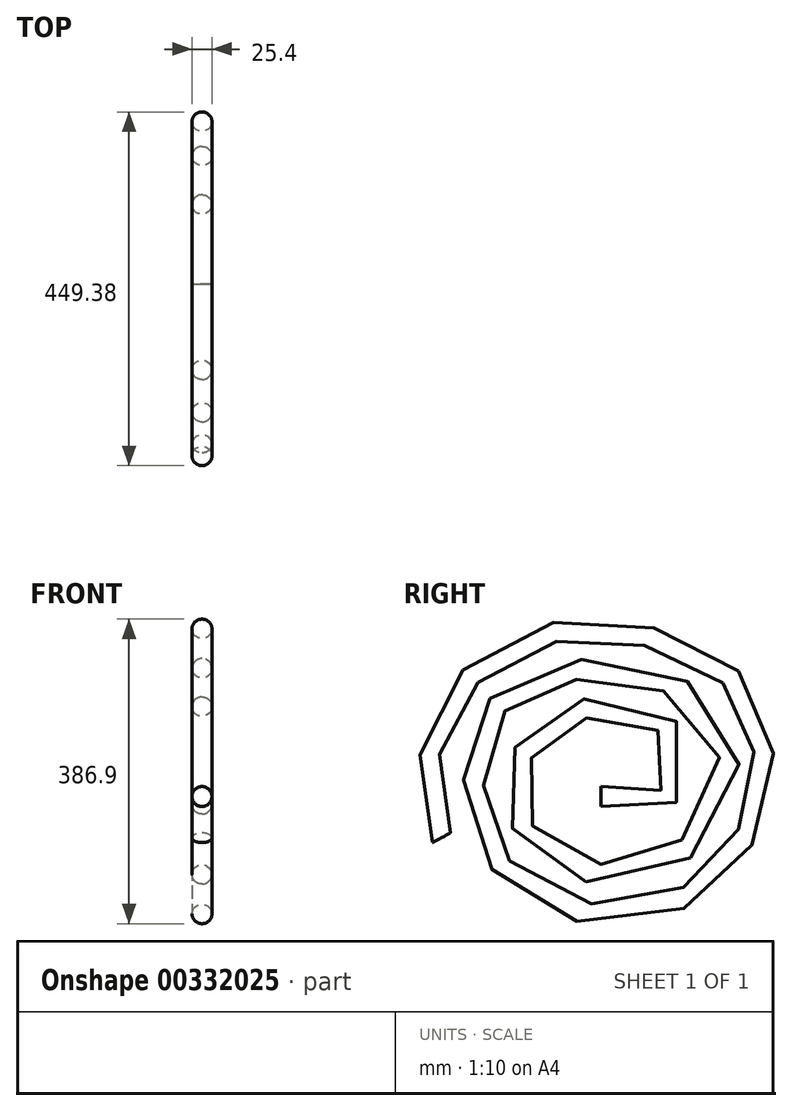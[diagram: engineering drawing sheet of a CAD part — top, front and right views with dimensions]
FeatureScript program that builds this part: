
annotation { "Feature Type Name" : "Feature", "Feature Type Description" : "" }
export const myFeature = defineFeature(function(context is Context, id is Id, definition is map)
    precondition{}
    {
        {
            var Q0;
            Q0=qCreatedBy(makeId("Front.planeOp"),FACE);
            var sketch = newSketch(context, id + "F0", { "sketchPlane" : qUnion([Q0])});
            skCircle(sketch, "E0", {"center": v(0, 0) * mm, "radius": 12.7 * mm});
            skSolve(sketch);
        }
        {
            var Q0;
            Q0=qCreatedBy(makeId("Right.planeOp"),FACE);
            var sketch = newSketch(context, id + "F1", { "sketchPlane" : qUnion([Q0])});
            skFitSpline(sketch, "E1", {"points": [v(0, 0) * mm, v(85.34, 0) * mm, v(87.12, 86.23) * mm, v(-48, 104.01) * mm, v(-106.68, 29.34) * mm, v(-76.45, -70.23) * mm, v(87.12, -80.9) * mm, v(160.02, 66.67) * mm, v(28.45, 160.9) * mm, v(-133.35, 114.68) * mm, v(-160.02, 0) * mm, v(-85.34, -127.13) * mm, v(101.35, -130.68) * mm, v(193.8, -25.78) * mm, v(192.02, 116.46) * mm, v(78.23, 198.25) * mm, v(-96.01, 198.25) * mm, v(-211.58, 82.68) * mm, v(-202.7, -52.45) * mm], "startDerivative": vector(2285.57, -593.16) * mm, "endDerivative": vector(626.22, -2485.68) * mm});
            skSolve(sketch);
        }
        {
            var Q0;
            Q0=makeQuery(id+"F0.imprint","IMPRINT",FACE,{"disambiguationData":[TD([[makeQuery(id+"F0.imprint","IMPRINT",EDGE,{"derivedFrom":sQuery(id+"F0.wireOp",EDGE,"E0")}),1.0]])]});
            var Q1;
            Q1=sQuery(id+"F1.wireOp",EDGE,"E1");
            sweep(context, id + "F2", {"profiles" : qUnion([Q0]), "path" : qUnion([Q1])});
        }
    });
